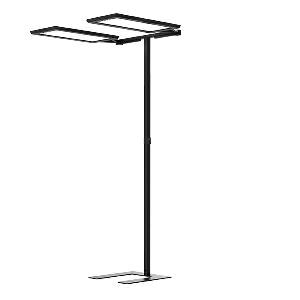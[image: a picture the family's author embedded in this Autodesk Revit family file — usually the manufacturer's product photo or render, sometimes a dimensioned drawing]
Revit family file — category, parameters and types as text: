
# Revit family: yara_doubleu_-_yus_2_15000_840_r_sw_cee_s0_c_114268000-00813286_4791
name_source: partatom
category: Lighting Fixtures
units: mm (PartAtom-declared; Revit-internal decimal feet)

## family parameters
Cut with Voids When Loaded = No
Host = Face
Light Source = No
Part Type = Normal
Room Calculation Point = No
Round Connector Dimension = Use Diameter
Shared = No

## types (1)
- YARA.doubleU - YUS 2/15000/840/R/SW/CEE/S0/C (1 x LED, 15000 lm, 4000K)
    Apparent Load = 214 VA
    Approval mark = CE
    CIE Flux Codes = 58 87 97 13 100
    Color Rendering = 80-89
    Color Temperature = 4000K
    Control Gear = Electronic ballast
    Default Elevation = 1800 mm
    Description = YUS 2/15000/840/R/SW/CEE/S0/C|Free-standing luminaire|light source: LED Cold white   |work equipment: Electronic ballast DALI|connected load: 220-240V, 50/60Hz|Power consumption: approx. 210 W|power factor: approx. 0,966|luminous flux: 30000 lm|luminous efficacy: 142 lm/W|light distribution: Direct/indirect|direct ratio: approx. 13 %|color rendering index (CRI): >= 80|chromaticity tolerance:  3 SDCM|technology: Presence and daylight sensor control (PIR)|operation: Wireless switch|luminaire body|material: Aluminium/plastic|surface: Powder coatet|colour: Black|lamp cover: Acrylic (PMMA)|tubular section|material: Steel tube|surface: Powder-coated|Form: Tubular section upright|colour of tubular section: Black|luminaire base|Form: C-form flat|weight (net): approx. 26.0 kg|mains lead: 3.00 m Mains plug CEE 7/VII|Fastening: Floor standing base|glare control: Conical prismatic screen|luminance(L65): <= 2700 cd/m|unified glare rating(4H 8H): <=  16|special features: App control, Asymmetric radiation, Direct and indirect lighting component with edge light and light guidetechnology for a homogeneous light exit, Flicker-free, Magnetic control panel, freely positionable, PIR movement and daylight sensor, TALK Bluetooth|Approval mark: VDE - ENEC|
    Frequency = 50 Hz, 60 Hz
    Height = 24 mm  [stored 0.0787402 ft]
    Lamp = 1 x LED
    Lamp Light Flux = 15000 lm
    Lamp count = 1
    Length = 690 mm
    Luminous efficacy = 140 lm/W
    Manufacturer = Waldmann
    ModVariant = No
    Model = 114268000-00813286
    Mounting Place = Floor
    Mounting Type = Freestanding
    Number of Poles = 1
    OnlyDefault = Yes
    Power Factor = 1
    Product Name = YARA.doubleU - YUS 2/15000/840/R/SW/CEE/S0/C
    Product group = Free standing luminaire
    ProductGroupID = 13
    Protection Class = Protection class I
    Protection Degree = IP 20
    RLX_Detail_Level = 1
    RlxData = <blob elided: 70893 chars, md5=9188474e>
    Socket = socket
    Standby Power = 0 W
    System Light Flux = 30000 lm
    System Power = 214 W
    Type Comments = Product without accessories
    Type Image = yus-r-sw-c.jpg
    URL = http://relux.com
    VarID = ---
    Voltage = 230 V
    Voltage Range = 220-240 V
    Weight = 0.00 kg
    Width = 358 mm

note: [stored X ft] marks values corroborated as IEEE doubles in the binary element streams (Revit-internal decimal feet)

## geometry (parser evidence)
native form markers: Blend x4, Sweep x21
no freeform markers — native parametric forms only
